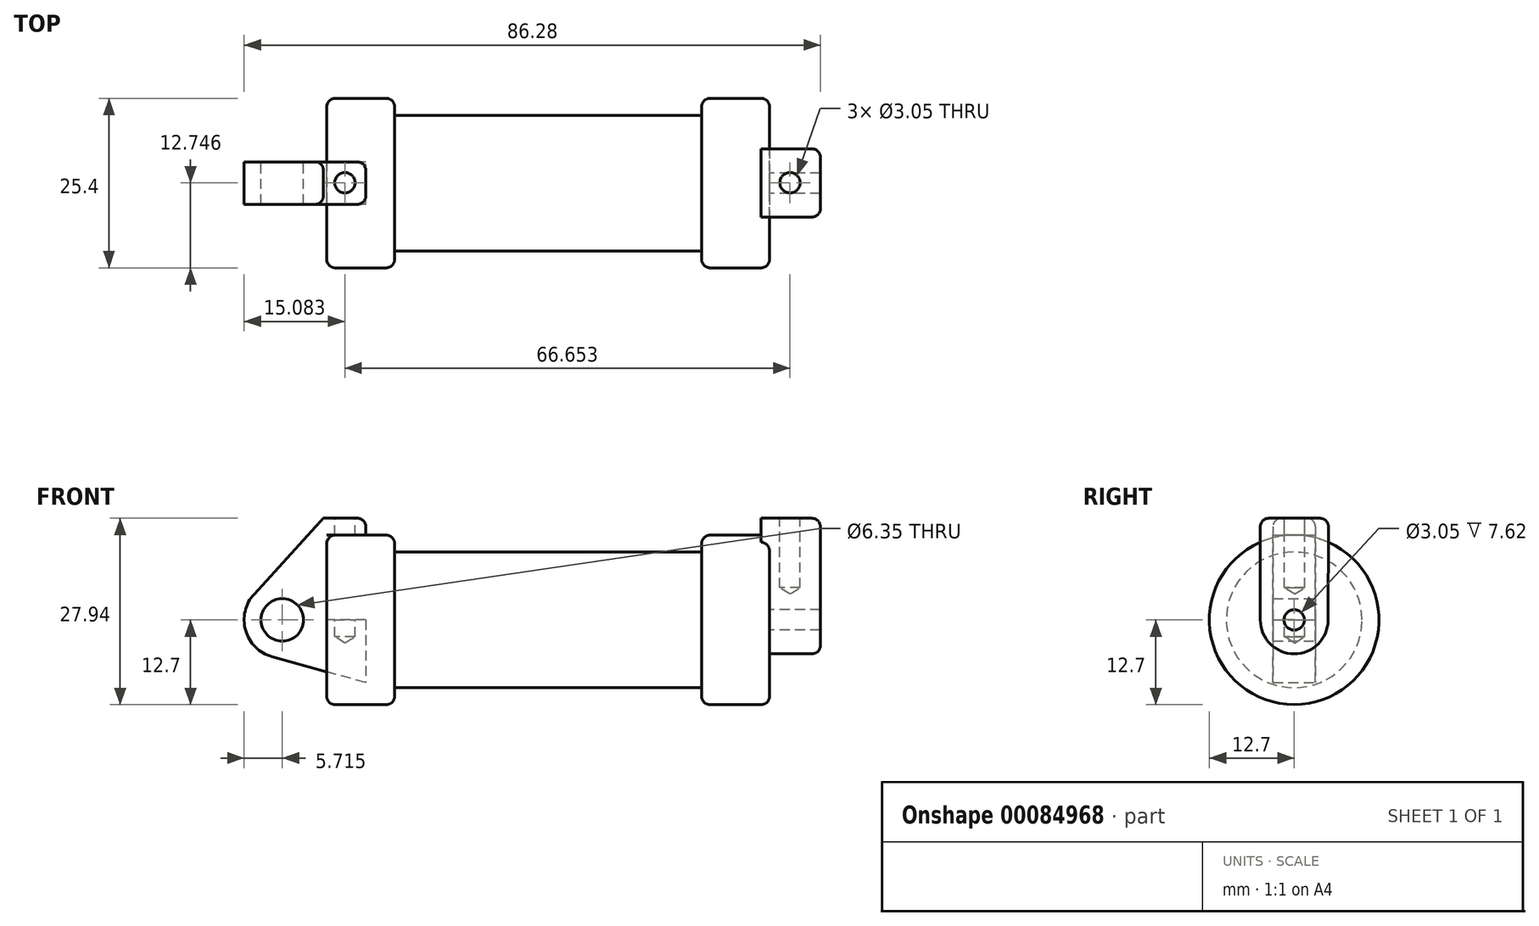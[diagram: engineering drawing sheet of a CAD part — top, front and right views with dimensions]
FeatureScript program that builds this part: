
annotation { "Feature Type Name" : "Feature", "Feature Type Description" : "" }
export const myFeature = defineFeature(function(context is Context, id is Id, definition is map)
    precondition{}
    {
        {
            var Q0;
            Q0=qCreatedBy(makeId("Front.planeOp"),FACE);
            var sketch = newSketch(context, id + "F0", { "sketchPlane" : qUnion([Q0])});
            skLineSegment(sketch, "E0", {"start": v(0, 0) * mm, "end": v(0, 12.7) * mm});
            skLineSegment(sketch, "E1", {"start": v(0, 12.7) * mm, "end": v(10.16, 12.7) * mm});
            skLineSegment(sketch, "E2", {"start": v(10.16, 12.7) * mm, "end": v(10.16, 10.16) * mm});
            skLineSegment(sketch, "E3", {"start": v(10.16, 10.16) * mm, "end": v(56.13, 10.16) * mm});
            skLineSegment(sketch, "E4", {"start": v(56.13, 10.16) * mm, "end": v(56.13, 12.7) * mm});
            skLineSegment(sketch, "E5", {"start": v(56.13, 12.7) * mm, "end": v(66.3, 12.7) * mm});
            skLineSegment(sketch, "E6", {"start": v(66.3, 12.7) * mm, "end": v(66.3, 0) * mm});
            skLineSegment(sketch, "E7", {"start": v(66.3, 0) * mm, "end": v(0, 0) * mm});
            skLineSegment(sketch, "E8", {"start": v(5.84, 15.24) * mm, "end": v(-0.5, 15.24) * mm});
            skLineSegment(sketch, "E9", {"start": v(-0.5, 15.24) * mm, "end": v(-10.88, 3.85) * mm});
            skLineSegment(sketch, "E10", {"start": v(0, 0) * mm, "end": v(-6.65, 0) * mm});
            skCircle(sketch, "E11", {"center": v(-6.65, 0) * mm, "radius": 5.72 * mm});
            skCircle(sketch, "E12", {"center": v(-6.65, 0) * mm, "radius": 3.18 * mm});
            skLineSegment(sketch, "E13", {"start": v(5.84, 15.24) * mm, "end": v(5.84, -9.4) * mm});
            skLineSegment(sketch, "E14", {"start": v(5.84, -9.4) * mm, "end": v(-8.18, -5.5) * mm});
            skSolve(sketch);
        }
        {
            var Q0;
            {var subQ0=sQuery(id+"F0.wireOp",EDGE,"E0");Q0=makeQuery(id+"F0.imprint","IMPRINT",FACE,{"disambiguationData":[TD([[makeQuery(id+"F0.imprint","IMPRINT",EDGE,{"derivedFrom":subQ0}),-1.0]])]});}
            var Q1;
            {var subQ0=sQuery(id+"F0.wireOp",EDGE,"E2");Q1=makeQuery(id+"F0.imprint","IMPRINT",FACE,{"disambiguationData":[TD([[makeQuery(id+"F0.imprint","IMPRINT",EDGE,{"derivedFrom":subQ0}),-1.0]])]});}
            var Q2;
            Q2=sQuery(id+"F0.wireOp",EDGE,"E7");
            revolve(context, id + "F1", {"entities" : qUnion([Q0, Q1]), "axis" : qUnion([Q2]), "revolveType" : RevolveType.FULL});
        }
        {
            var Q0;
            {var subQ0=sQuery(id+"F0.wireOp",EDGE,"E14");Q0=makeQuery(id+"F0.imprint","IMPRINT",FACE,{"disambiguationData":[TD([[makeQuery(id+"F0.imprint","IMPRINT",EDGE,{"derivedFrom":subQ0}),-1.0]])]});}
            var Q1;
            {var subQ3=sQuery(id+"F0.wireOp",EDGE,"E0");Q1=makeQuery(id+"F0.imprint","IMPRINT",FACE,{"disambiguationData":[TD([[makeQuery(id+"F0.imprint","IMPRINT",EDGE,{"derivedFrom":subQ3}),1.0]])]});}
            var Q2;
            {var subQ4=sQuery(id+"F0.wireOp",EDGE,"E12");Q2=makeQuery(id+"F0.imprint","IMPRINT",FACE,{"disambiguationData":[TD([[makeQuery(id+"F0.imprint","IMPRINT",EDGE,{"derivedFrom":subQ4}),-1.0]])]});}
            var Q3;
            Q3=sQuery(id+"F0.wireOp",EDGE,"E8");
            var Q4;
            Q4=sQuery(id+"F0.wireOp",EDGE,"E13");
            var Q5;
            Q5=sQuery(id+"F0.wireOp",EDGE,"E14");
            var Q6;
            Q6=sQuery(id+"F0.wireOp",EDGE,"E11");
            var Q7;
            Q7=sQuery(id+"F0.wireOp",EDGE,"E12");
            var Q8;
            Q8=sQuery(id+"F0.wireOp",EDGE,"E9");
            extrude(context, id + "F2", {"entities" : qUnion([Q0, Q1, Q2]), "surfaceEntities" : qUnion([Q3, Q4, Q5, Q6, Q7, Q8]), "endBound" : BoundingType.SYMMETRIC, "depth" : 6.35 * mm});
        }
        {
            var Q0;
            Q0=makeQuery(id+"F1.opRevolve","SWEPT_FACE",FACE,{"disambiguationData":[OSD([sQuery(id+"F0.wireOp",EDGE,"E6")])]});
            var sketch = newSketch(context, id + "F3", { "sketchPlane" : qUnion([Q0])});
            skCircle(sketch, "E15", {"center": v(0, 0) * mm, "radius": 5.08 * mm});
            skCircle(sketch, "E16", {"center": v(0, 0) * mm, "radius": 1.52 * mm});
            skLineSegment(sketch, "E17", {"start": v(-5.08, 0) * mm, "end": v(-5.08, 15.22) * mm});
            skLineSegment(sketch, "E18", {"start": v(-5.08, 15.22) * mm, "end": v(5.14, 15.22) * mm});
            skLineSegment(sketch, "E19", {"start": v(5.14, 15.22) * mm, "end": v(5.08, -0.02) * mm});
            skSolve(sketch);
        }
        {
            var Q0;
            Q0=qSketchRegion(id+"F3",true);
            extrude(context, id + "F4", {"entities" : qUnion([Q0]), "operationType" : NewBodyOperationType.ADD, "depth" : 7.62 * mm});
        }
        {
            var Q0;
            Q0=makeQuery(id+"F4.opExtrude","CAP_FACE",FACE,{"disambiguationData":[OSD([sQuery(id+"F3.wireOp",EDGE,"E15"),sQuery(id+"F3.wireOp",EDGE,"E16"),sQuery(id+"F3.wireOp",EDGE,"E17"),sQuery(id+"F3.wireOp",EDGE,"E18"),sQuery(id+"F3.wireOp",EDGE,"E19")])],"isStart":true});
            extrude(context, id + "F5", {"entities" : qUnion([Q0]), "operationType" : NewBodyOperationType.ADD, "depth" : 1.27 * mm});
        }
        {
            var Q0;
            {var subQ0=sQuery(id+"F3.wireOp",EDGE,"E18");Q0=makeQuery(id+"F5.boolean.opBoolean","MERGE",FACE,{"derivedFrom":[makeQuery(id+"F4.opExtrude","SWEPT_FACE",FACE,{"disambiguationData":[OSD([subQ0])]}),makeQuery(id+"F5.opExtrude","SWEPT_FACE",FACE,{"disambiguationData":[OSD([subQ0])]})]});}
            var sketch = newSketch(context, id + "F6", { "sketchPlane" : qUnion([Q0])});
            skCircle(sketch, "E20", {"center": v(69.37, 0.05) * mm, "radius": 1.52 * mm});
            skSolve(sketch);
        }
        {
            var Q0;
            Q0=sQuery(id+"F6.wireOp",VERTEX,"E20.center");
            var Q1;
            Q1=makeQuery(id+"F1.opRevolve","SWEPT_BODY",BODY,{"disambiguationData":[OSD([sQuery(id+"F0.wireOp",EDGE,"E0"),sQuery(id+"F0.wireOp",EDGE,"E1"),sQuery(id+"F0.wireOp",EDGE,"E2"),sQuery(id+"F0.wireOp",EDGE,"E3"),sQuery(id+"F0.wireOp",EDGE,"E4"),sQuery(id+"F0.wireOp",EDGE,"E5"),sQuery(id+"F0.wireOp",EDGE,"E6"),sQuery(id+"F0.wireOp",EDGE,"E7")])]});
            hole(context, id + "F7", {"style" : HoleStyle.SIMPLE, "endStyle" : HoleEndStyle.BLIND, "holeDiameter" : 3.05 * mm, "holeDepth" : 10.4 * mm, "locations" : qUnion([Q0]), "scope" : qUnion([Q1])});
        }
        {
            var Q0;
            Q0=makeQuery(id+"F2.opExtrude","SWEPT_FACE",FACE,{"disambiguationData":[OSD([sQuery(id+"F0.wireOp",EDGE,"E8")])]});
            var sketch = newSketch(context, id + "F8", { "sketchPlane" : qUnion([Q0])});
            skCircle(sketch, "E21", {"center": v(2.71, 0.05) * mm, "radius": 1.52 * mm});
            skSolve(sketch);
        }
        {
            var Q0;
            Q0=sQuery(id+"F8.wireOp",VERTEX,"E21.center");
            var Q1;
            Q1=makeQuery(id+"F2.opExtrude","SWEPT_BODY",BODY,{"disambiguationData":[OSD([sQuery(id+"F0.wireOp",EDGE,"E0"),sQuery(id+"F0.wireOp",EDGE,"E1"),sQuery(id+"F0.wireOp",EDGE,"E7"),sQuery(id+"F0.wireOp",EDGE,"E8"),sQuery(id+"F0.wireOp",EDGE,"E9"),sQuery(id+"F0.wireOp",EDGE,"E11"),sQuery(id+"F0.wireOp",EDGE,"E12"),sQuery(id+"F0.wireOp",EDGE,"E13"),sQuery(id+"F0.wireOp",EDGE,"E14")])]});
            hole(context, id + "F9", {"style" : HoleStyle.SIMPLE, "endStyle" : HoleEndStyle.BLIND, "holeDiameter" : 3.05 * mm, "holeDepth" : 17.78 * mm, "locations" : qUnion([Q0]), "scope" : qUnion([Q1])});
        }
        {
            var Q0;
            Q0=makeQuery(id+"F1.opRevolve","SWEPT_EDGE",EDGE,{"disambiguationData":[OSD([sQuery(id+"F0.wireOp",EDGE,"E1"),sQuery(id+"F0.wireOp",EDGE,"E2")])]});
            var Q1;
            Q1=makeQuery(id+"F1.opRevolve","SWEPT_EDGE",EDGE,{"disambiguationData":[OSD([sQuery(id+"F0.wireOp",EDGE,"E4"),sQuery(id+"F0.wireOp",EDGE,"E5")])]});
            fillet(context, id + "F10", {"entities" : qUnion([Q0, Q1]), "radius" : 1.27 * mm, "tangentPropagation" : true, "allowEdgeOverflow" : false});
        }
        {
            var Q0;
            Q0=makeQuery(id+"F1.opRevolve","SWEPT_EDGE",EDGE,{"disambiguationData":[OSD([sQuery(id+"F0.wireOp",EDGE,"E0"),sQuery(id+"F0.wireOp",EDGE,"E1")])]});
            var Q1;
            Q1=makeQuery(id+"F4.boolean.opBoolean","SPLIT",EDGE,{"disambiguationData":[OD(1.0)],"derivedFrom":makeQuery(id+"F1.opRevolve","SWEPT_EDGE",EDGE,{"disambiguationData":[OSD([sQuery(id+"F0.wireOp",EDGE,"E5"),sQuery(id+"F0.wireOp",EDGE,"E6")])]})});
            fillet(context, id + "F11", {"entities" : qUnion([Q0, Q1]), "radius" : 1.27 * mm, "tangentPropagation" : true, "allowEdgeOverflow" : false});
        }
        {
            var Q0;
            {var subQ0=sQuery(id+"F3.wireOp",EDGE,"E18");var subQ1=sQuery(id+"F3.wireOp",EDGE,"E17");Q0=makeQuery(id+"F5.boolean.opBoolean","MERGE",EDGE,{"derivedFrom":[makeQuery(id+"F4.opExtrude","SWEPT_EDGE",EDGE,{"disambiguationData":[OSD([subQ1,subQ0])]}),makeQuery(id+"F5.opExtrude","SWEPT_EDGE",EDGE,{"disambiguationData":[OSD([subQ1,subQ0])]})]});}
            var Q1;
            Q1=makeQuery(id+"F4.opExtrude","CAP_EDGE",EDGE,{"disambiguationData":[OSD([sQuery(id+"F3.wireOp",EDGE,"E17")])],"isStart":false});
            fillet(context, id + "F12", {"entities" : qUnion([Q0, Q1]), "radius" : 1.27 * mm, "tangentPropagation" : true, "allowEdgeOverflow" : false});
        }
        {
            var Q0;
            {var subQ0=sQuery(id+"F3.wireOp",EDGE,"E19");var subQ1=sQuery(id+"F3.wireOp",EDGE,"E18");Q0=makeQuery(id+"F5.boolean.opBoolean","MERGE",EDGE,{"derivedFrom":[makeQuery(id+"F4.opExtrude","SWEPT_EDGE",EDGE,{"disambiguationData":[OSD([subQ1,subQ0])]}),makeQuery(id+"F5.opExtrude","SWEPT_EDGE",EDGE,{"disambiguationData":[OSD([subQ1,subQ0])]})]});}
            var Q1;
            {var subQ0=sQuery(id+"F3.wireOp",EDGE,"E19");Q1=makeQuery(id+"F12.opFillet","BLEND_EDGE",EDGE,{"blendedFrom":[makeQuery(id+"F4.opExtrude","CAP_EDGE",EDGE,{"disambiguationData":[OSD([subQ0])],"isStart":false}),makeQuery(id+"F4.opExtrude","CAP_FACE",FACE,{"disambiguationData":[OSD([sQuery(id+"F3.wireOp",EDGE,"E15"),sQuery(id+"F3.wireOp",EDGE,"E16"),sQuery(id+"F3.wireOp",EDGE,"E17"),sQuery(id+"F3.wireOp",EDGE,"E18"),subQ0])],"isStart":false})],"blendedInto":[makeQuery(id+"F4.opExtrude","CAP_FACE",FACE,{"disambiguationData":[OSD([sQuery(id+"F3.wireOp",EDGE,"E15"),sQuery(id+"F3.wireOp",EDGE,"E16"),sQuery(id+"F3.wireOp",EDGE,"E17"),sQuery(id+"F3.wireOp",EDGE,"E18"),subQ0])],"isStart":false})]});}
            var Q2;
            Q2=makeQuery(id+"F2.opExtrude","CAP_EDGE",EDGE,{"disambiguationData":[OSD([sQuery(id+"F0.wireOp",EDGE,"E8")])],"isStart":false});
            var Q3;
            Q3=makeQuery(id+"F2.opExtrude","SWEPT_EDGE",EDGE,{"disambiguationData":[OSD([sQuery(id+"F0.wireOp",EDGE,"E8"),sQuery(id+"F0.wireOp",EDGE,"E13")])]});
            var Q4;
            Q4=makeQuery(id+"F2.opExtrude","CAP_EDGE",EDGE,{"disambiguationData":[OSD([sQuery(id+"F0.wireOp",EDGE,"E8")])],"isStart":true});
            var Q5;
            {var subQ0=sQuery(id+"F0.wireOp",EDGE,"E13");Q5=makeQuery(id+"F2.opExtrude","CAP_EDGE",EDGE,{"disambiguationData":[OSD([subQ0]),TDD([makeQuery(id+"F0.imprint","IMPRINT",EDGE,{"disambiguationData":[TD([[makeQuery(id+"F0.imprint","INTERSECT",VERTEX,{"derivedFrom":[sQuery(id+"F0.wireOp",EDGE,"E8"),subQ0]}),-1.0]])],"derivedFrom":subQ0})])],"isStart":false});}
            var Q6;
            {var subQ0=sQuery(id+"F0.wireOp",EDGE,"E13");Q6=makeQuery(id+"F2.opExtrude","CAP_EDGE",EDGE,{"disambiguationData":[OSD([subQ0]),TDD([makeQuery(id+"F0.imprint","IMPRINT",EDGE,{"disambiguationData":[TD([[makeQuery(id+"F0.imprint","INTERSECT",VERTEX,{"derivedFrom":[sQuery(id+"F0.wireOp",EDGE,"E8"),subQ0]}),-1.0]])],"derivedFrom":subQ0})])],"isStart":true});}
            fillet(context, id + "F13", {"entities" : qUnion([Q0, Q1, Q2, Q3, Q4, Q5, Q6]), "radius" : 1.27 * mm, "tangentPropagation" : true, "allowEdgeOverflow" : false});
        }
    });
